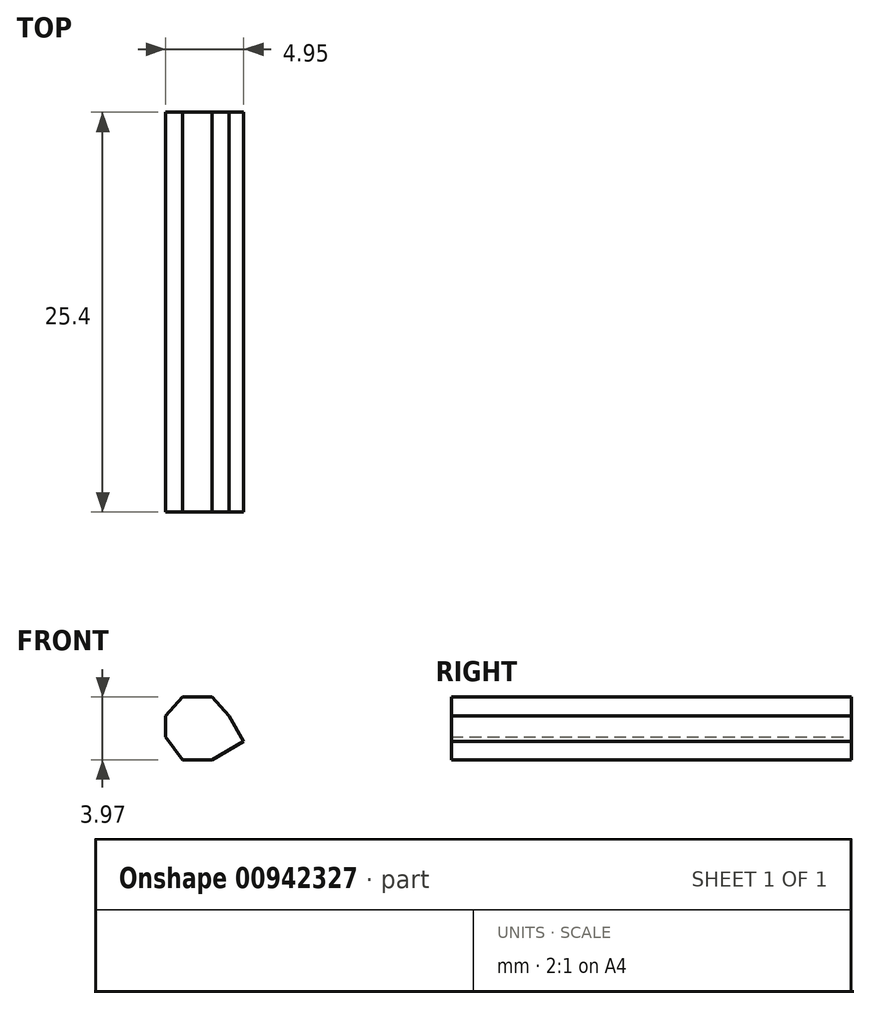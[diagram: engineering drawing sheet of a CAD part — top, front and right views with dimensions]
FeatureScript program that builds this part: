
annotation { "Feature Type Name" : "Feature", "Feature Type Description" : "" }
export const myFeature = defineFeature(function(context is Context, id is Id, definition is map)
    precondition{}
    {
        {
            var Q0;
            Q0=qCreatedBy(makeId("Front.planeOp"),FACE);
            var sketch = newSketch(context, id + "F0", { "sketchPlane" : qUnion([Q0])});
            skLineSegment(sketch, "E0", {"start": v(-34.5, 40.37) * mm, "end": v(-34.5, 41.7) * mm});
            skLineSegment(sketch, "E1", {"start": v(-34.5, 41.7) * mm, "end": v(-33.42, 42.91) * mm});
            skLineSegment(sketch, "E2", {"start": v(-33.42, 42.91) * mm, "end": v(-31.55, 42.91) * mm});
            skLineSegment(sketch, "E3", {"start": v(-31.55, 42.91) * mm, "end": v(-30.48, 41.7) * mm});
            skLineSegment(sketch, "E4", {"start": v(-30.48, 41.7) * mm, "end": v(-29.54, 40.1) * mm});
            skLineSegment(sketch, "E5", {"start": v(-29.54, 40.1) * mm, "end": v(-31.55, 38.94) * mm});
            skLineSegment(sketch, "E6", {"start": v(-31.55, 38.94) * mm, "end": v(-33.42, 38.94) * mm});
            skLineSegment(sketch, "E7", {"start": v(-33.42, 38.94) * mm, "end": v(-34.5, 40.37) * mm});
            skSolve(sketch);
        }
        {
            var Q0;
            Q0=makeQuery(id+"F0.imprint","IMPRINT",FACE,{"disambiguationData":[TD([[makeQuery(id+"F0.imprint","IMPRINT",EDGE,{"derivedFrom":sQuery(id+"F0.wireOp",EDGE,"E0")}),-1.0]])]});
            extrude(context, id + "F1", {"entities" : qUnion([Q0]), "depth" : 25.4 * mm, "offsetDistance" : 25.4 * mm});
        }
    });
